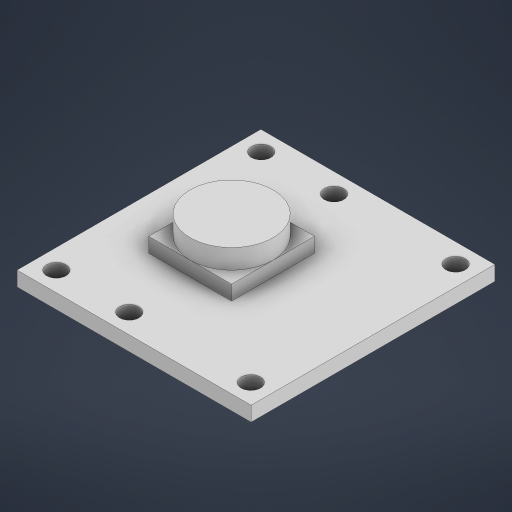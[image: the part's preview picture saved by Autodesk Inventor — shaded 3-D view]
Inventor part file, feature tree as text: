
AUTODESK INVENTOR PART (.ipt)
format: ipt  version: 2024 (Build 280153000, 153)  size: 227,328 bytes
history: native  units: mm
features: extrude x3, other x1, sketch x1
ambient origin geometry x8: Origin, YZ Plane, XZ Plane, XY Plane, X Axis, Y Axis, Z Axis, Center Point
bodies: Body1 (feature_tree)
feature tree (5):
  other  "솔리드1"
  sketch  "스케치1"
  extrude  "돌출1"  Depth=24.0mm
  extrude  "돌출2"  Depth=25.0mm
  extrude  "돌출3"  Depth=2.0mm
